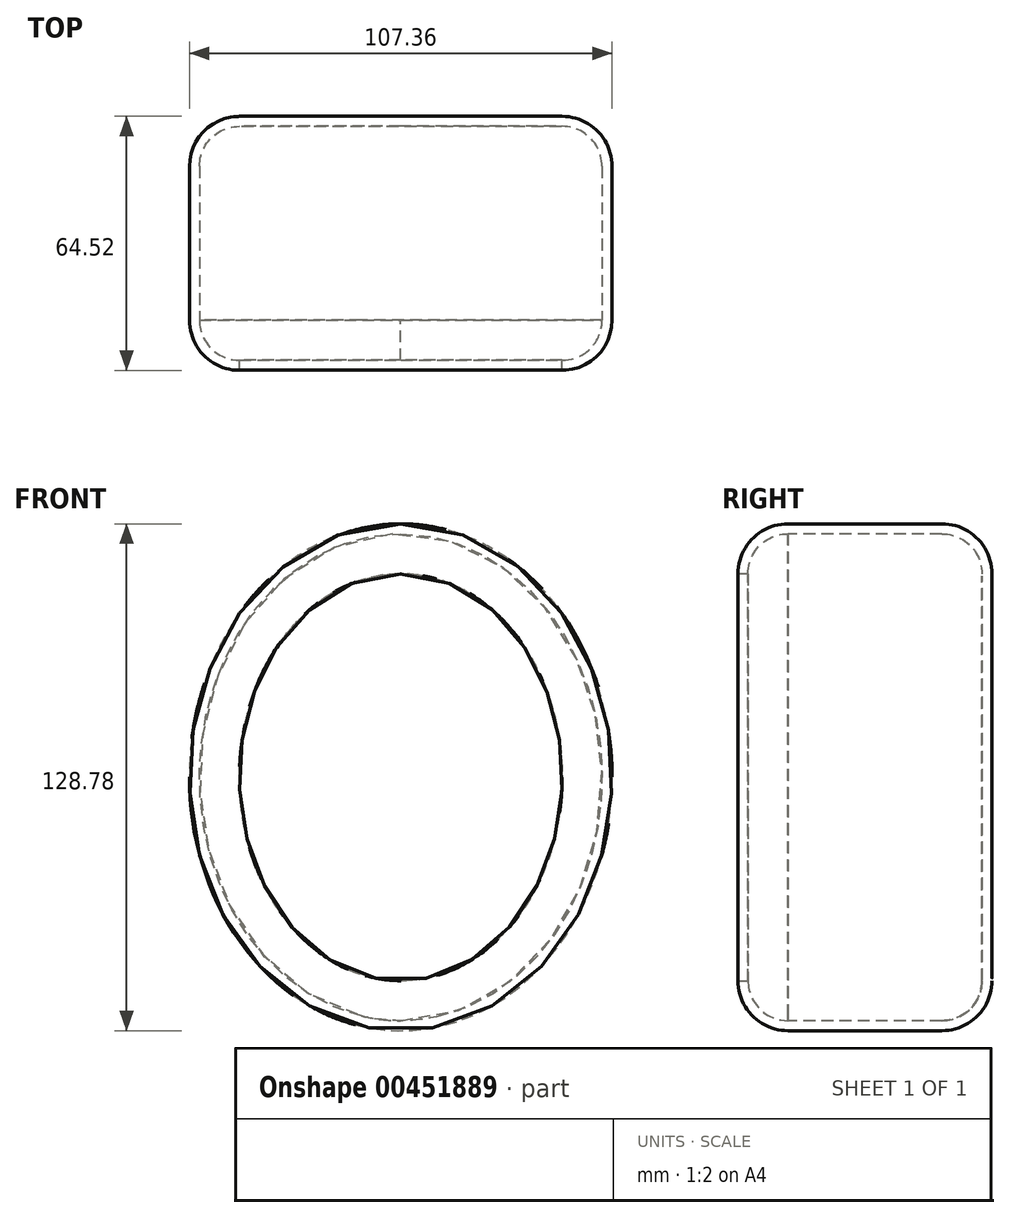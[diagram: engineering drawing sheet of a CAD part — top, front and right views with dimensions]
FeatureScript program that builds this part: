
annotation { "Feature Type Name" : "Feature", "Feature Type Description" : "" }
export const myFeature = defineFeature(function(context is Context, id is Id, definition is map)
    precondition{}
    {
        {
            var Q0;
            Q0=qCreatedBy(makeId("Front.planeOp"),FACE);
            var sketch = newSketch(context, id + "F0", { "sketchPlane" : qUnion([Q0])});
            skEllipse(sketch, "E0", {"center": v(0, 0) * mm, "majorRadius": 64.39 * mm, "minorRadius": 53.68 * mm, "majorAxis": v(0, 1)});
            skSolve(sketch);
        }
        {
            var Q0;
            Q0 = qSketchRegion(id + "F0", true);
            extrude(context, id + "F1", {"entities" : qUnion([Q0]), "depth" : 39.12 * mm, "hasSecondDirection" : true, "secondDirectionOppositeDirection" : true, "secondDirectionDepth" : 25.4 * mm});
        }
        {
            var Q0;
            Q0=makeQuery(id+"F1.opExtrude","CAP_EDGE",EDGE,{"disambiguationData":[OSD([sQuery(id+"F0.wireOp",EDGE,"E0")])],"isStart":false});
            var Q1;
            Q1=makeQuery(id+"F1.opExtrude","CAP_EDGE",EDGE,{"disambiguationData":[OSD([sQuery(id+"F0.wireOp",EDGE,"E0")])],"isStart":true});
            fillet(context, id + "F2", {"entities" : qUnion([Q0, Q1]), "radius" : 12.7 * mm, "tangentPropagation" : true, "allowEdgeOverflow" : false});
        }
        {
            var Q0;
            Q0=makeQuery(id+"F1.opExtrude","CAP_FACE",FACE,{"disambiguationData":[OSD([sQuery(id+"F0.wireOp",EDGE,"E0")])],"isStart":false});
            shell(context, id + "F3", {"entities" : qUnion([Q0]), "thickness" : 2.54 * mm});
        }
    });
